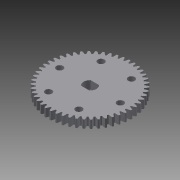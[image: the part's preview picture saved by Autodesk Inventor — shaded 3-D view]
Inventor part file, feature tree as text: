
AUTODESK INVENTOR PART (.ipt)
format: ipt  version: 2013 (Build 170138000, 138)  size: 435,712 bytes
history: native  units: in
note: dims shown in document units (in); Inventor stores cm internally (conversion verified against a paired STEP export)
features: extrude x1, sketch x1
ambient origin geometry x8: Origin, YZ Plane, XZ Plane, XY Plane, X Axis, Y Axis, Z Axis, Center Point
bodies: Solid1 (feature_tree)
feature tree (2):
  extrude  "Extrusion1"  Depth=0.1968in
  sketch  "Sketch1"  dims[d0=0.2955in d2=0.1968in d3=0.1968in d4=0.2598in d5=1.175in d6=0.5996in d7=0.1894in d8=0.25in d9=0.0in]
